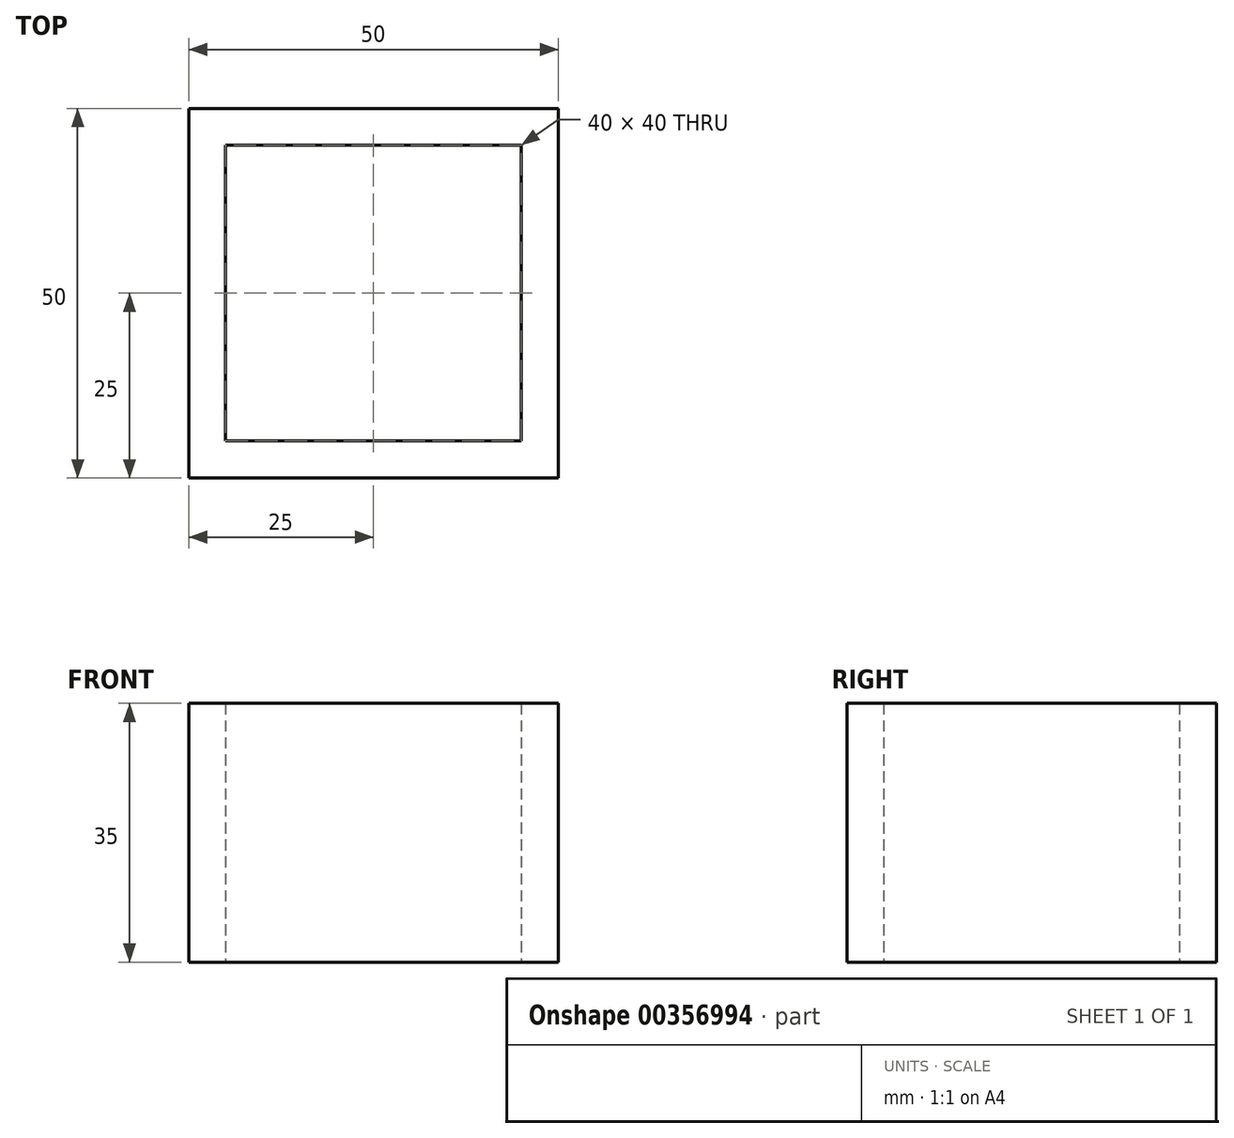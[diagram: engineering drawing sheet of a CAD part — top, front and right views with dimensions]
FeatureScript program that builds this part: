
annotation { "Feature Type Name" : "Feature", "Feature Type Description" : "" }
export const myFeature = defineFeature(function(context is Context, id is Id, definition is map)
    precondition{}
    {
        {
            var Q0;
            Q0=qCreatedBy(makeId("Top.planeOp"),FACE);
            var sketch = newSketch(context, id + "F0", { "sketchPlane" : qUnion([Q0])});
            skLineSegment(sketch, "E0.bottom", {"start": v(0, 0) * mm, "end": v(50, 0) * mm});
            skLineSegment(sketch, "E0.top", {"start": v(0, 50) * mm, "end": v(50, 50) * mm});
            skLineSegment(sketch, "E0.left", {"start": v(0, 0) * mm, "end": v(0, 50) * mm});
            skLineSegment(sketch, "E0.right", {"start": v(50, 0) * mm, "end": v(50, 50) * mm});
            skLineSegment(sketch, "E1.bottom", {"start": v(45, 45) * mm, "end": v(5, 45) * mm});
            skLineSegment(sketch, "E1.top", {"start": v(45, 5) * mm, "end": v(5, 5) * mm});
            skLineSegment(sketch, "E1.left", {"start": v(45, 45) * mm, "end": v(45, 5) * mm});
            skLineSegment(sketch, "E1.right", {"start": v(5, 45) * mm, "end": v(5, 5) * mm});
            skPoint(sketch, "E1.middle", {"position": v(25, 25) * mm});
            skLineSegment(sketch, "E2", {"start": v(25, 25) * mm, "end": v(25, 50) * mm, "construction": true});
            skLineSegment(sketch, "E3", {"start": v(25, 25) * mm, "end": v(0, 25) * mm, "construction": true});
            skSolve(sketch);
        }
        {
            var Q0;
            Q0=makeQuery(id+"F0.imprint","IMPRINT",FACE,{"disambiguationData":[TD([[makeQuery(id+"F0.imprint","IMPRINT",EDGE,{"derivedFrom":sQuery(id+"F0.wireOp",EDGE,"E0.bottom")}),1.0]])]});
            extrude(context, id + "F1", {"entities" : qUnion([Q0]), "depth" : 35 * mm});
        }
    });
